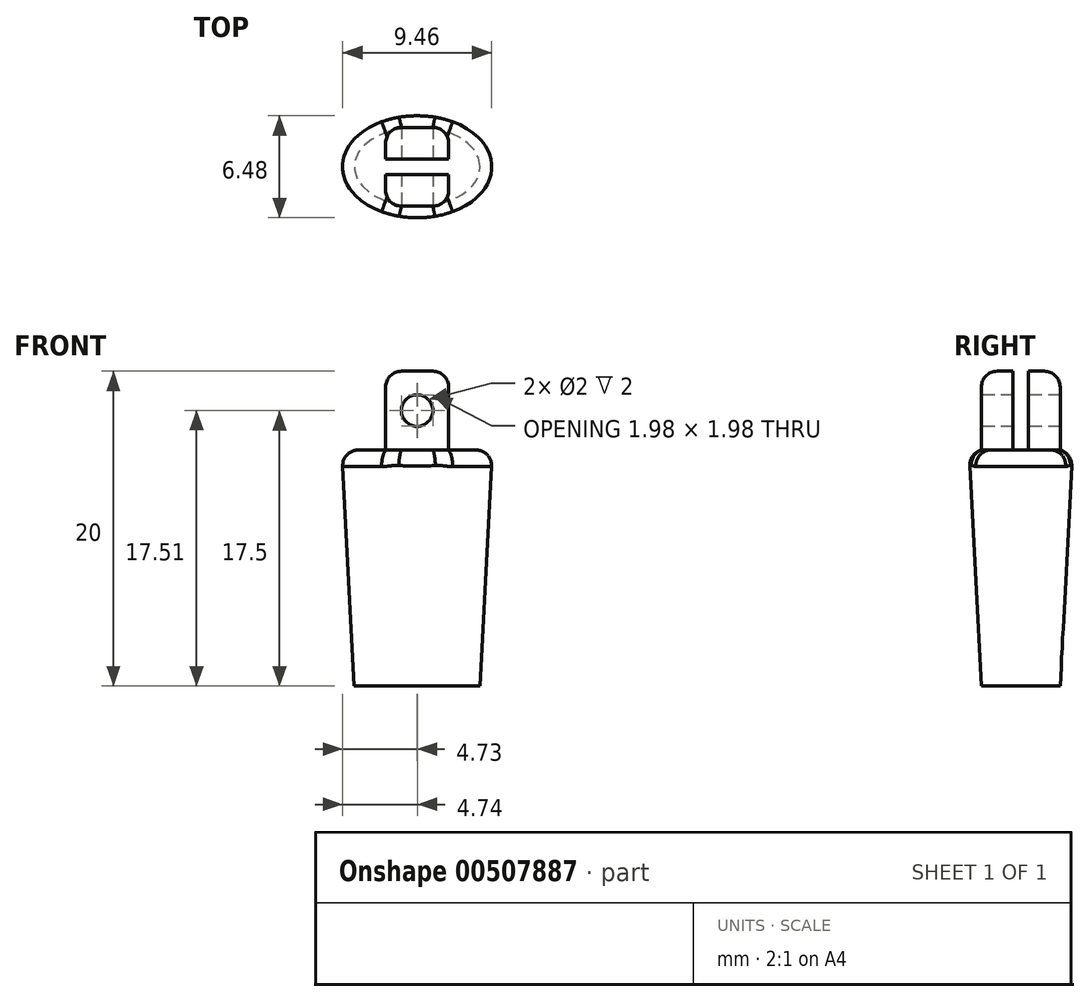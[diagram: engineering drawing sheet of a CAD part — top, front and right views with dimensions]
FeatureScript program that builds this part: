
annotation { "Feature Type Name" : "Feature", "Feature Type Description" : "" }
export const myFeature = defineFeature(function(context is Context, id is Id, definition is map)
    precondition{}
    {
        {
            var Q0;
            Q0=qCreatedBy(makeId("Top.planeOp"),FACE);
            var sketch = newSketch(context, id + "F0", { "sketchPlane" : qUnion([Q0])});
            skEllipse(sketch, "E0", {"center": v(0, 0) * mm, "majorRadius": 4 * mm, "minorRadius": 2.5 * mm, "majorAxis": v(-1, 0)});
            skSolve(sketch);
        }
        {
            var Q0;
            Q0=makeQuery(id+"F0.imprint","IMPRINT",FACE,{"disambiguationData":[TD([[makeQuery(id+"F0.imprint","IMPRINT",EDGE,{"derivedFrom":sQuery(id+"F0.wireOp",EDGE,"E0")}),1.0]])]});
            extrude(context, id + "F1", {"entities" : qUnion([Q0]), "depth" : 15 * mm, "offsetDistance" : 25 * mm, "hasDraft" : true, "draftAngle" : 3 * degree});
        }
        {
            var Q0;
            Q0=makeQuery(id+"F1.opExtrude","CAP_FACE",FACE,{"disambiguationData":[OSD([sQuery(id+"F0.wireOp",EDGE,"E0")])],"isStart":false});
            var sketch = newSketch(context, id + "F2", { "sketchPlane" : qUnion([Q0])});
            skLineSegment(sketch, "E1", {"start": v(0, 0) * mm, "end": v(0, 0.5) * mm, "construction": true});
            skLineSegment(sketch, "E2", {"start": v(0, 0.5) * mm, "end": v(2, 0.5) * mm});
            skLineSegment(sketch, "E3", {"start": v(2, 0.5) * mm, "end": v(2, 2.5) * mm});
            skLineSegment(sketch, "E4", {"start": v(2, 2.5) * mm, "end": v(-2, 2.5) * mm});
            skLineSegment(sketch, "E5", {"start": v(-2, 2.5) * mm, "end": v(-2, 0.5) * mm});
            skLineSegment(sketch, "E6", {"start": v(-2, 0.5) * mm, "end": v(0, 0.5) * mm});
            skLineSegment(sketch, "E7", {"start": v(0, 0) * mm, "end": v(4.79, 0) * mm, "construction": true});
            skLineSegment(sketch, "E8.MirrorCS", {"start": v(2, -2.5) * mm, "end": v(-2, -2.5) * mm});
            skLineSegment(sketch, "E9.MirrorCS", {"start": v(-2, -2.5) * mm, "end": v(-2, -0.5) * mm});
            skLineSegment(sketch, "E10.MirrorCS", {"start": v(2, -0.5) * mm, "end": v(2, -2.5) * mm});
            skLineSegment(sketch, "E11.MirrorCS", {"start": v(0, -0.5) * mm, "end": v(2, -0.5) * mm});
            skLineSegment(sketch, "E12.MirrorCS", {"start": v(-2, -0.5) * mm, "end": v(0, -0.5) * mm});
            skSolve(sketch);
        }
        {
            var Q0;
            Q0=makeQuery(id+"F2.imprint","IMPRINT",FACE,{"disambiguationData":[TD([[makeQuery(id+"F2.imprint","IMPRINT",EDGE,{"derivedFrom":sQuery(id+"F2.wireOp",EDGE,"E2")}),1.0]])]});
            extrude(context, id + "F3", {"entities" : qUnion([Q0]), "operationType" : NewBodyOperationType.ADD, "depth" : 5 * mm, "offsetDistance" : 25 * mm});
        }
        {
            var Q0;
            Q0=makeQuery(id+"F2.imprint","IMPRINT",FACE,{"disambiguationData":[TD([[makeQuery(id+"F2.imprint","IMPRINT",EDGE,{"derivedFrom":sQuery(id+"F2.wireOp",EDGE,"E8.MirrorCS")}),-1.0]])]});
            extrude(context, id + "F4", {"entities" : qUnion([Q0]), "operationType" : NewBodyOperationType.ADD, "depth" : 5 * mm, "offsetDistance" : 25 * mm});
        }
        {
            var Q0;
            Q0=makeQuery(id+"F4.opExtrude","SWEPT_EDGE",EDGE,{"disambiguationData":[OSD([sQuery(id+"F2.wireOp",EDGE,"E8.MirrorCS"),sQuery(id+"F2.wireOp",EDGE,"E9.MirrorCS")])]});
            var Q1;
            Q1=makeQuery(id+"F4.opExtrude","SWEPT_EDGE",EDGE,{"disambiguationData":[OSD([sQuery(id+"F2.wireOp",EDGE,"E8.MirrorCS"),sQuery(id+"F2.wireOp",EDGE,"E10.MirrorCS")])]});
            var Q2;
            Q2=makeQuery(id+"F3.opExtrude","SWEPT_EDGE",EDGE,{"disambiguationData":[OSD([sQuery(id+"F2.wireOp",EDGE,"E3"),sQuery(id+"F2.wireOp",EDGE,"E4")])]});
            var Q3;
            Q3=makeQuery(id+"F3.opExtrude","SWEPT_EDGE",EDGE,{"disambiguationData":[OSD([sQuery(id+"F2.wireOp",EDGE,"E4"),sQuery(id+"F2.wireOp",EDGE,"E5")])]});
            fillet(context, id + "F5", {"entities" : qUnion([Q0, Q1, Q2, Q3]), "radius" : 1 * mm, "tangentPropagation" : true, "allowEdgeOverflow" : false});
        }
        {
            var Q0;
            Q0=makeQuery(id+"F4.opExtrude","SWEPT_FACE",FACE,{"disambiguationData":[OSD([sQuery(id+"F2.wireOp",EDGE,"E8.MirrorCS")])]});
            var sketch = newSketch(context, id + "F6", { "sketchPlane" : qUnion([Q0])});
            skLineSegment(sketch, "E13", {"start": v(0, 15) * mm, "end": v(0, 17.5) * mm, "construction": true});
            skPoint(sketch, "E13.endSnap0", {"position": v(0, 20) * mm});
            skCircle(sketch, "E14", {"center": v(0, 17.5) * mm, "radius": 1 * mm});
            skSolve(sketch);
        }
        {
            var Q0;
            {var subQ0=sQuery(id+"F6.wireOp",EDGE,"E14");var subQ1=sQuery(id+"F2.wireOp",EDGE,"E8.MirrorCS");var subQ2=makeQuery(id+"F4.opExtrude","SWEPT_FACE",FACE,{"disambiguationData":[OSD([subQ1])]});var subQ3=makeQuery(id+"F6.imprint","INTERSECT",VERTEX,{"derivedFrom":[makeQuery(id+"F5.opFillet","BLEND_EDGE",EDGE,{"blendedFrom":[makeQuery(id+"F4.opExtrude","SWEPT_EDGE",EDGE,{"disambiguationData":[OSD([subQ1,sQuery(id+"F2.wireOp",EDGE,"E10.MirrorCS")])]}),subQ2],"blendedInto":[subQ2]}),subQ0]});Q0=makeQuery(id+"F6.imprint","IMPRINT",FACE,{"disambiguationData":[TD([[makeQuery(id+"F6.imprint","IMPRINT",EDGE,{"disambiguationData":[TD([[subQ3,-1.0]])],"derivedFrom":subQ0}),1.0]])]});}
            var Q1;
            Q1=sQuery(id+"F6.wireOp",EDGE,"E14");
            var Q2;
            Q2=makeQuery(id+"F3.opExtrude","SWEPT_FACE",FACE,{"disambiguationData":[OSD([sQuery(id+"F2.wireOp",EDGE,"E4")])]});
            extrude(context, id + "F7", {"entities" : qUnion([Q0]), "operationType" : NewBodyOperationType.REMOVE, "surfaceEntities" : qUnion([Q1]), "endBound" : BoundingType.UP_TO_SURFACE, "oppositeDirection" : true, "depth" : 25 * mm, "endBoundEntityFace" : qUnion([Q2]), "offsetDistance" : 25 * mm});
        }
        {
            var Q0;
            Q0=makeQuery(id+"F4.opExtrude","CAP_EDGE",EDGE,{"disambiguationData":[OSD([sQuery(id+"F2.wireOp",EDGE,"E9.MirrorCS")])],"isStart":false});
            var Q1;
            Q1=makeQuery(id+"F3.opExtrude","CAP_EDGE",EDGE,{"disambiguationData":[OSD([sQuery(id+"F2.wireOp",EDGE,"E5")])],"isStart":false});
            fillet(context, id + "F8", {"entities" : qUnion([Q0, Q1]), "radius" : 1 * mm, "tangentPropagation" : true, "allowEdgeOverflow" : false});
        }
        {
            var Q0;
            Q0=makeQuery(id+"F1.opExtrude","CAP_EDGE",EDGE,{"disambiguationData":[OSD([sQuery(id+"F0.wireOp",EDGE,"E0")])],"isStart":false});
            fillet(context, id + "F9", {"entities" : qUnion([Q0]), "radius" : 1 * mm, "tangentPropagation" : true, "allowEdgeOverflow" : false});
        }
    });
